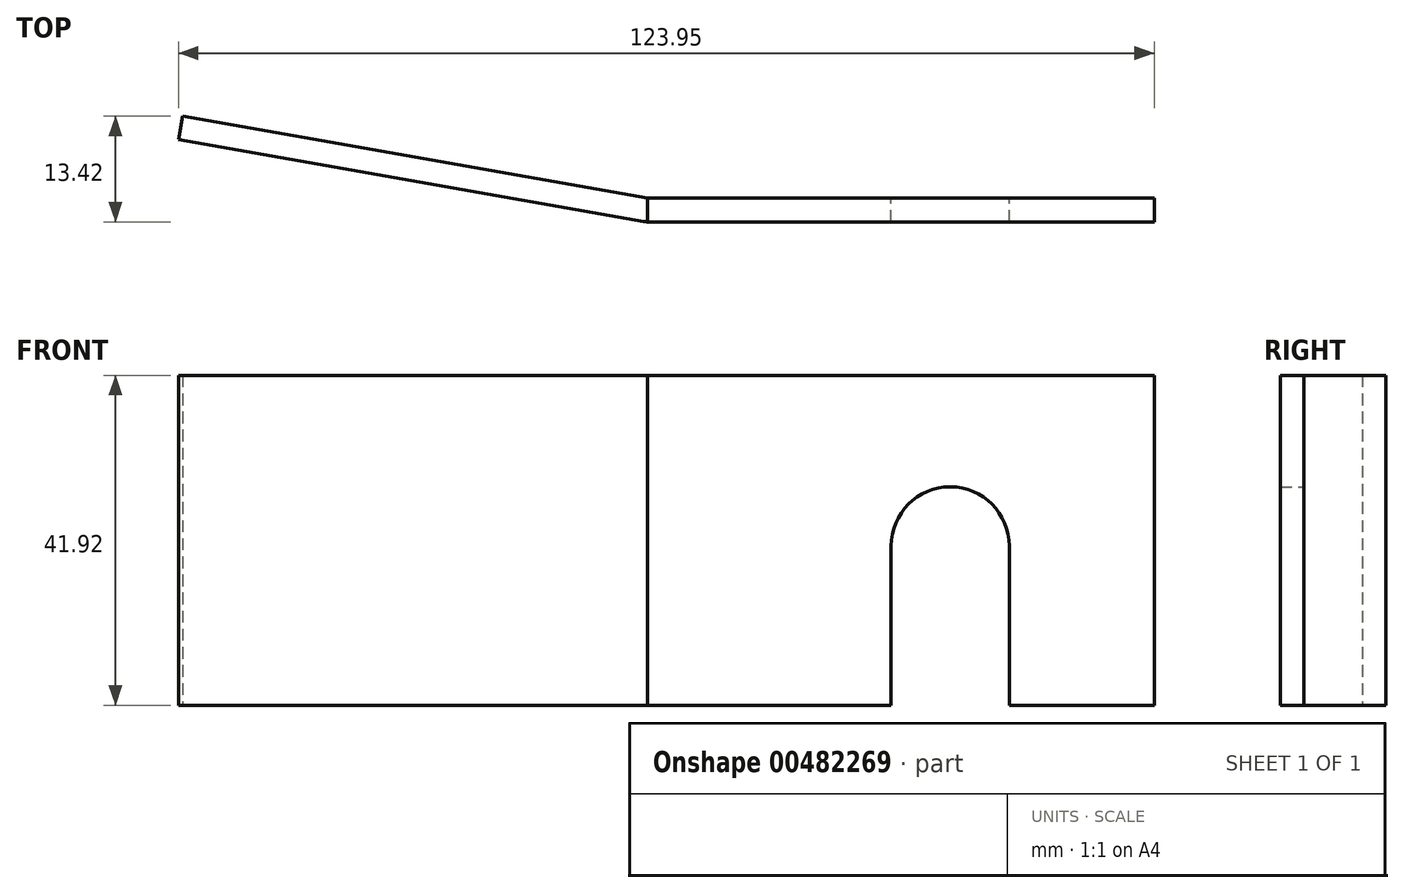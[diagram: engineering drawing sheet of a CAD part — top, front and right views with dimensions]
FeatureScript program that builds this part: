
annotation { "Feature Type Name" : "Feature", "Feature Type Description" : "" }
export const myFeature = defineFeature(function(context is Context, id is Id, definition is map)
    precondition{}
    {
        {
            var Q0;
            Q0=qCreatedBy(makeId("Front.planeOp"),FACE);
            var sketch = newSketch(context, id + "F0", { "sketchPlane" : qUnion([Q0])});
            skArc(sketch, "E0", {"start": v(7.5, 0) * mm, "mid": v(0, 7.5) * mm, "end": v(-7.5, 0) * mm});
            skLineSegment(sketch, "E1", {"start": v(-38.43, 21.67) * mm, "end": v(25.9, 21.67) * mm});
            skLineSegment(sketch, "E2", {"start": v(25.9, 21.67) * mm, "end": v(25.9, -20.25) * mm});
            skLineSegment(sketch, "E3", {"start": v(25.9, -20.25) * mm, "end": v(7.5, -20.25) * mm});
            skLineSegment(sketch, "E4", {"start": v(7.5, -20.25) * mm, "end": v(7.5, 0) * mm});
            skLineSegment(sketch, "E5", {"start": v(-38.43, 21.67) * mm, "end": v(-38.43, -20.25) * mm});
            skLineSegment(sketch, "E6", {"start": v(-38.43, -20.25) * mm, "end": v(-7.5, -20.25) * mm});
            skLineSegment(sketch, "E7", {"start": v(-7.5, -20.25) * mm, "end": v(-7.5, 0) * mm});
            skSolve(sketch);
        }
        {
            var Q0;
            Q0=makeQuery(id+"F0.imprint","IMPRINT",FACE,{"disambiguationData":[TD([[makeQuery(id+"F0.imprint","IMPRINT",EDGE,{"derivedFrom":sQuery(id+"F0.wireOp",EDGE,"E0")}),-1.0]])]});
            extrude(context, id + "F1", {"entities" : qUnion([Q0]), "depth" : 3 * mm});
        }
        {
            var Q0;
            Q0=qCreatedBy(makeId("Top.planeOp"),FACE);
            var sketch = newSketch(context, id + "F2", { "sketchPlane" : qUnion([Q0])});
            skLineSegment(sketch, "E8", {"start": v(-38.43, 0) * mm, "end": v(-97.52, 10.42) * mm});
            skLineSegment(sketch, "E9", {"start": v(-97.52, 10.42) * mm, "end": v(-98.04, 7.46) * mm});
            skLineSegment(sketch, "E10", {"start": v(-98.04, 7.46) * mm, "end": v(-38.95, -2.95) * mm});
            skArc(sketch, "E11", {"start": v(-38.95, -2.95) * mm, "mid": v(-38.7, -2.99) * mm, "end": v(-38.43, -3) * mm});
            skLineSegment(sketch, "E12", {"start": v(-38.43, 0) * mm, "end": v(-38.43, -3) * mm});
            skSolve(sketch);
        }
        {
            var Q0;
            Q0 = qSketchRegion(id + "F2", true);
            var Q1;
            Q1=makeQuery(id+"F1.opExtrude","SWEPT_FACE",FACE,{"disambiguationData":[OSD([sQuery(id+"F0.wireOp",EDGE,"E1")])]});
            var Q2;
            Q2=makeQuery(id+"F1.opExtrude","SWEPT_FACE",FACE,{"disambiguationData":[OSD([sQuery(id+"F0.wireOp",EDGE,"E6")])]});
            extrude(context, id + "F3", {"entities" : qUnion([Q0]), "endBound" : BoundingType.UP_TO_SURFACE, "endBoundEntityFace" : qUnion([Q1]), "depth" : 25 * mm, "hasSecondDirection" : true, "secondDirectionBound" : SecondDirectionBoundingType.UP_TO_SURFACE, "secondDirectionOppositeDirection" : true, "secondDirectionBoundEntityFace" : qUnion([Q2]), "secondDirectionDepth" : 25 * mm});
        }
    });
